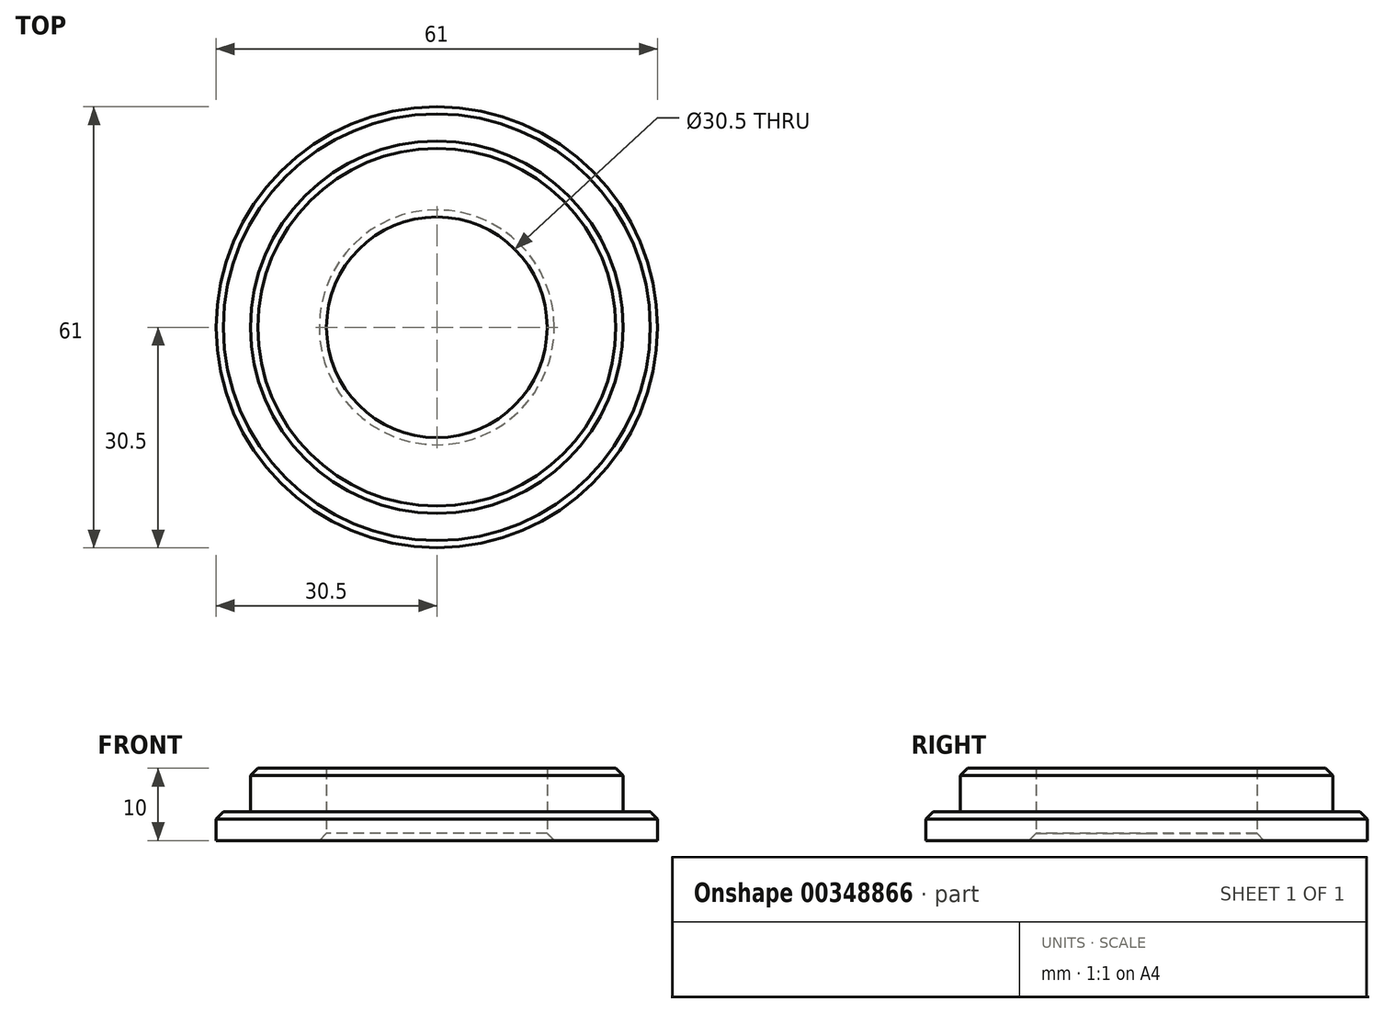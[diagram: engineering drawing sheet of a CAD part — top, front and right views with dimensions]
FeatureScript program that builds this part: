
annotation { "Feature Type Name" : "Feature", "Feature Type Description" : "" }
export const myFeature = defineFeature(function(context is Context, id is Id, definition is map)
    precondition{}
    {
        {
            var Q0;
            Q0=qCreatedBy(makeId("Top.planeOp"),FACE);
            var sketch = newSketch(context, id + "F0", { "sketchPlane" : qUnion([Q0])});
            skCircle(sketch, "E0", {"center": v(0, 0) * mm, "radius": 15.25 * mm});
            skCircle(sketch, "E1", {"center": v(0, 0) * mm, "radius": 30.5 * mm});
            skSolve(sketch);
        }
        {
            var Q0;
            Q0=qSketchRegion(id+"F0",true);
            extrude(context, id + "F1", {"entities" : qUnion([Q0]), "depth" : 4 * mm});
        }
        {
            var Q0;
            Q0=makeQuery(id+"F1.opExtrude","CAP_FACE",FACE,{"disambiguationData":[OSD([sQuery(id+"F0.wireOp",EDGE,"E0"),sQuery(id+"F0.wireOp",EDGE,"E1")])],"isStart":false});
            var sketch = newSketch(context, id + "F2", { "sketchPlane" : qUnion([Q0])});
            skCircle(sketch, "E2", {"center": v(0, 0) * mm, "radius": 25.75 * mm});
            skCircle(sketch, "E3", {"center": v(0, 0) * mm, "radius": 15.25 * mm});
            skSolve(sketch);
        }
        {
            var Q0;
            Q0=qSketchRegion(id+"F2",true);
            extrude(context, id + "F3", {"entities" : qUnion([Q0]), "operationType" : NewBodyOperationType.ADD, "depth" : 6 * mm});
        }
        {
            var Q0;
            Q0=makeQuery(id+"F3.opExtrude","CAP_EDGE",EDGE,{"disambiguationData":[OSD([sQuery(id+"F2.wireOp",EDGE,"E2")])],"isStart":false});
            var Q1;
            Q1=makeQuery(id+"F1.opExtrude","CAP_EDGE",EDGE,{"disambiguationData":[OSD([sQuery(id+"F0.wireOp",EDGE,"E1")])],"isStart":false});
            chamfer(context, id + "F4", {"entities" : qUnion([Q0, Q1]), "width" : 1 * mm, "tangentPropagation" : true});
        }
        {
            var Q0;
            Q0=makeQuery(id+"F1.opExtrude","CAP_EDGE",EDGE,{"disambiguationData":[OSD([sQuery(id+"F0.wireOp",EDGE,"E0")])],"isStart":true});
            chamfer(context, id + "F5", {"entities" : qUnion([Q0]), "width" : 1 * mm, "tangentPropagation" : true});
        }
    });
